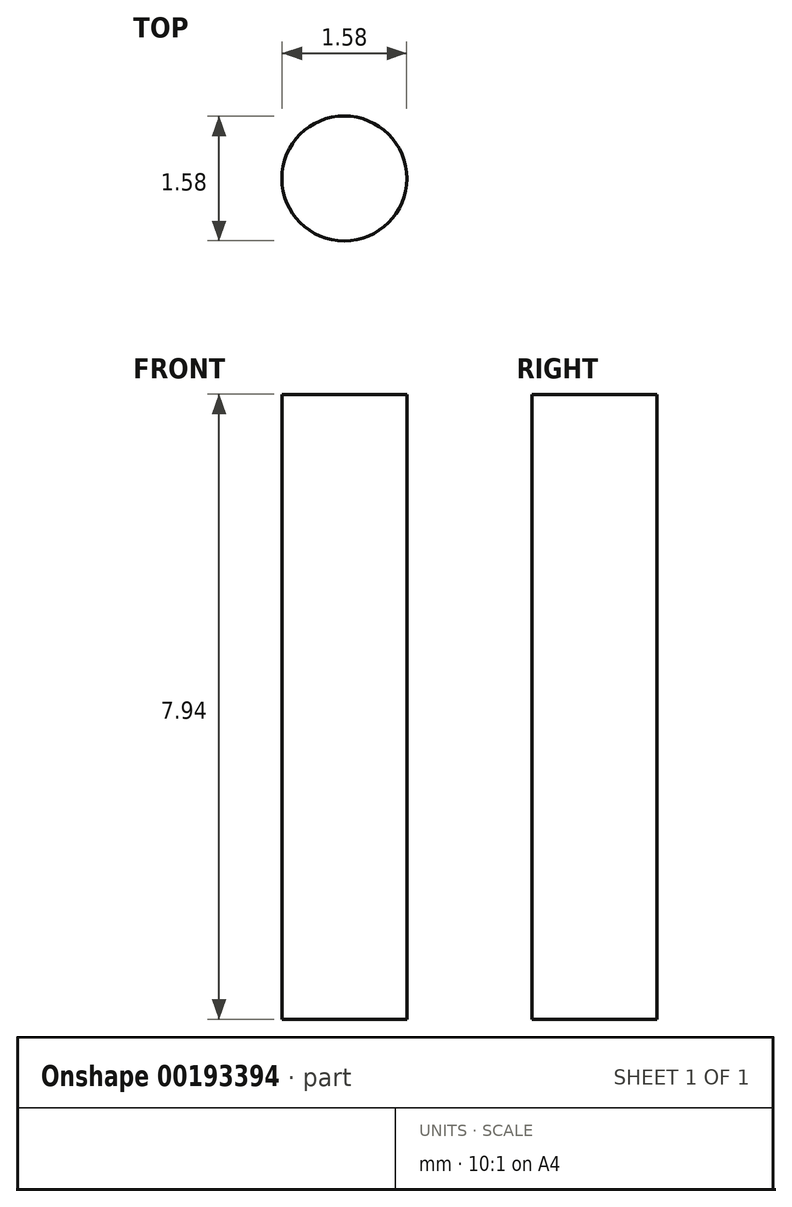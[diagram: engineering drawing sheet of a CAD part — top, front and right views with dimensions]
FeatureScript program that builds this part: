
annotation { "Feature Type Name" : "Feature", "Feature Type Description" : "" }
export const myFeature = defineFeature(function(context is Context, id is Id, definition is map)
    precondition{}
    {
        {
            var Q0;
            Q0=qCreatedBy(makeId("Top.planeOp"),FACE);
            var sketch = newSketch(context, id + "F0", { "sketchPlane" : qUnion([Q0])});
            skCircle(sketch, "E0", {"center": v(0, 0) * mm, "radius": 0.8 * mm});
            skSolve(sketch);
        }
        {
            var Q0;
            Q0 = qSketchRegion(id + "F0", true);
            extrude(context, id + "F1", {"entities" : qUnion([Q0]), "depth" : 7.94 * mm});
        }
    });
